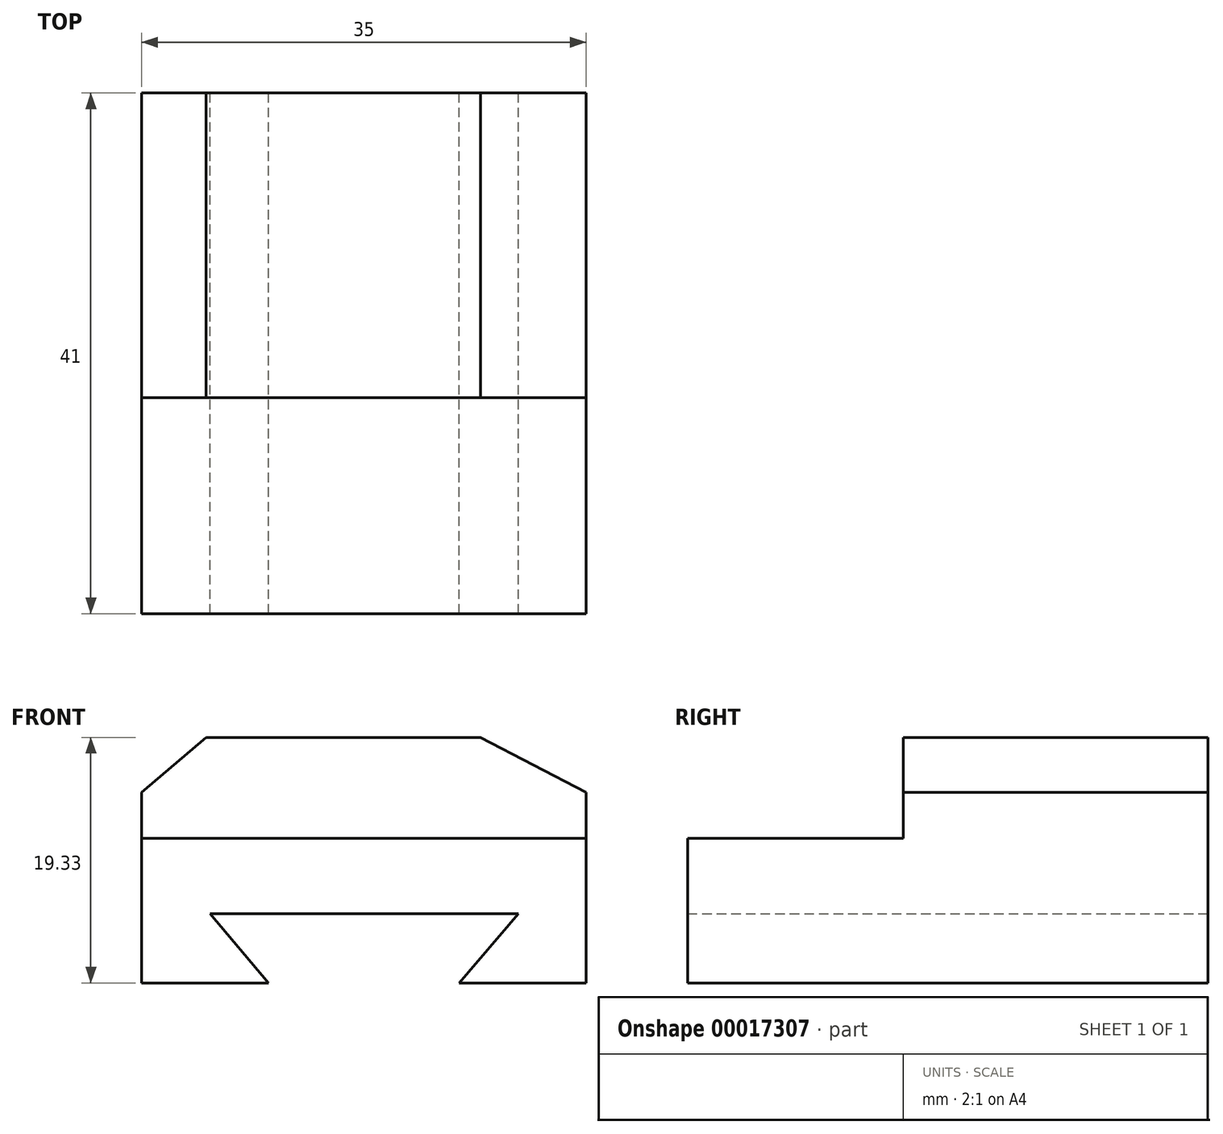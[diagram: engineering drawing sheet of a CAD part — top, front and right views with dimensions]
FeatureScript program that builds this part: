
annotation { "Feature Type Name" : "Feature", "Feature Type Description" : "" }
export const myFeature = defineFeature(function(context is Context, id is Id, definition is map)
    precondition{}
    {
        {
            var Q0;
            Q0=qCreatedBy(makeId("Front.planeOp"),FACE);
            var sketch = newSketch(context, id + "F0", { "sketchPlane" : qUnion([Q0])});
            skLineSegment(sketch, "E0.bottom", {"start": v(-20.76, 13.63) * mm, "end": v(0.88, 13.63) * mm});
            skLineSegment(sketch, "E0.top", {"start": v(-25.81, -5.7) * mm, "end": v(9.19, -5.7) * mm});
            skLineSegment(sketch, "E0.left", {"start": v(-25.81, 4.3) * mm, "end": v(-25.81, -5.7) * mm});
            skLineSegment(sketch, "E0.right", {"start": v(9.19, 4.3) * mm, "end": v(9.19, -5.7) * mm});
            skLineSegment(sketch, "E1", {"start": v(-15.81, -5.7) * mm, "end": v(-20.43, -0.25) * mm});
            skLineSegment(sketch, "E2", {"start": v(-20.43, -0.25) * mm, "end": v(3.87, -0.25) * mm});
            skLineSegment(sketch, "E3", {"start": v(3.87, -0.25) * mm, "end": v(-0.81, -5.7) * mm});
            skLineSegment(sketch, "E4", {"start": v(9.19, 4.3) * mm, "end": v(9.19, 9.3) * mm});
            skLineSegment(sketch, "E5", {"start": v(-25.81, 4.3) * mm, "end": v(-25.81, 9.3) * mm});
            skLineSegment(sketch, "E6", {"start": v(-25.81, 9.3) * mm, "end": v(-20.76, 13.63) * mm});
            skLineSegment(sketch, "E7", {"start": v(9.19, 9.3) * mm, "end": v(0.88, 13.63) * mm});
            skSolve(sketch);
        }
        {
            var Q0;
            Q0=makeQuery(id+"F0.imprint","IMPRINT",FACE,{"disambiguationData":[TD([[makeQuery(id+"F0.imprint","IMPRINT",EDGE,{"derivedFrom":sQuery(id+"F0.wireOp",EDGE,"E0.bottom")}),-1.0]])]});
            extrude(context, id + "F1", {"entities" : qUnion([Q0]), "depth" : 23 * mm});
        }
        {
            var Q0;
            Q0=makeQuery(id+"F1.opExtrude","CAP_FACE",FACE,{"disambiguationData":[OSD([sQuery(id+"F0.wireOp",EDGE,"E0.bottom"),sQuery(id+"F0.wireOp",EDGE,"E0.top"),sQuery(id+"F0.wireOp",EDGE,"E0.left"),sQuery(id+"F0.wireOp",EDGE,"E0.right"),sQuery(id+"F0.wireOp",EDGE,"e0260b30-796b-45fa-b522-223277c4a52c"),sQuery(id+"F0.wireOp",EDGE,"d1fabc08-ca8a-4516-b8e1-47e82b197ed7"),sQuery(id+"F0.wireOp",EDGE,"E1"),sQuery(id+"F0.wireOp",EDGE,"E2"),sQuery(id+"F0.wireOp",EDGE,"E3")])],"isStart":false});
            extrude(context, id + "F2", {"entities" : qUnion([Q0]), "operationType" : NewBodyOperationType.ADD, "depth" : 18 * mm});
        }
        {
            var Q0;
            Q0=makeQuery(id+"F2.opExtrude","CAP_FACE",FACE,{"disambiguationData":[OSD([sQuery(id+"F0.wireOp",EDGE,"E0.bottom"),sQuery(id+"F0.wireOp",EDGE,"E0.top"),sQuery(id+"F0.wireOp",EDGE,"E0.left"),sQuery(id+"F0.wireOp",EDGE,"E0.right"),sQuery(id+"F0.wireOp",EDGE,"e0260b30-796b-45fa-b522-223277c4a52c"),sQuery(id+"F0.wireOp",EDGE,"d1fabc08-ca8a-4516-b8e1-47e82b197ed7"),sQuery(id+"F0.wireOp",EDGE,"E1"),sQuery(id+"F0.wireOp",EDGE,"E2"),sQuery(id+"F0.wireOp",EDGE,"E3")])],"isStart":false});
            var sketch = newSketch(context, id + "F3", { "sketchPlane" : qUnion([Q0])});
            skLineSegment(sketch, "E8", {"start": v(-25.81, 5.7) * mm, "end": v(9.19, 5.7) * mm});
            skSolve(sketch);
        }
        {
            var Q0;
            Q0=makeQuery(id+"F3.imprint","IMPRINT",FACE,{"disambiguationData":[TD([[makeQuery(id+"F3.imprint","IMPRINT",EDGE,{"derivedFrom":sQuery(id+"F3.wireOp",EDGE,"E8")}),1.0]])]});
            extrude(context, id + "F4", {"entities" : qUnion([Q0]), "operationType" : NewBodyOperationType.REMOVE, "oppositeDirection" : true, "depth" : 17 * mm});
        }
    });
